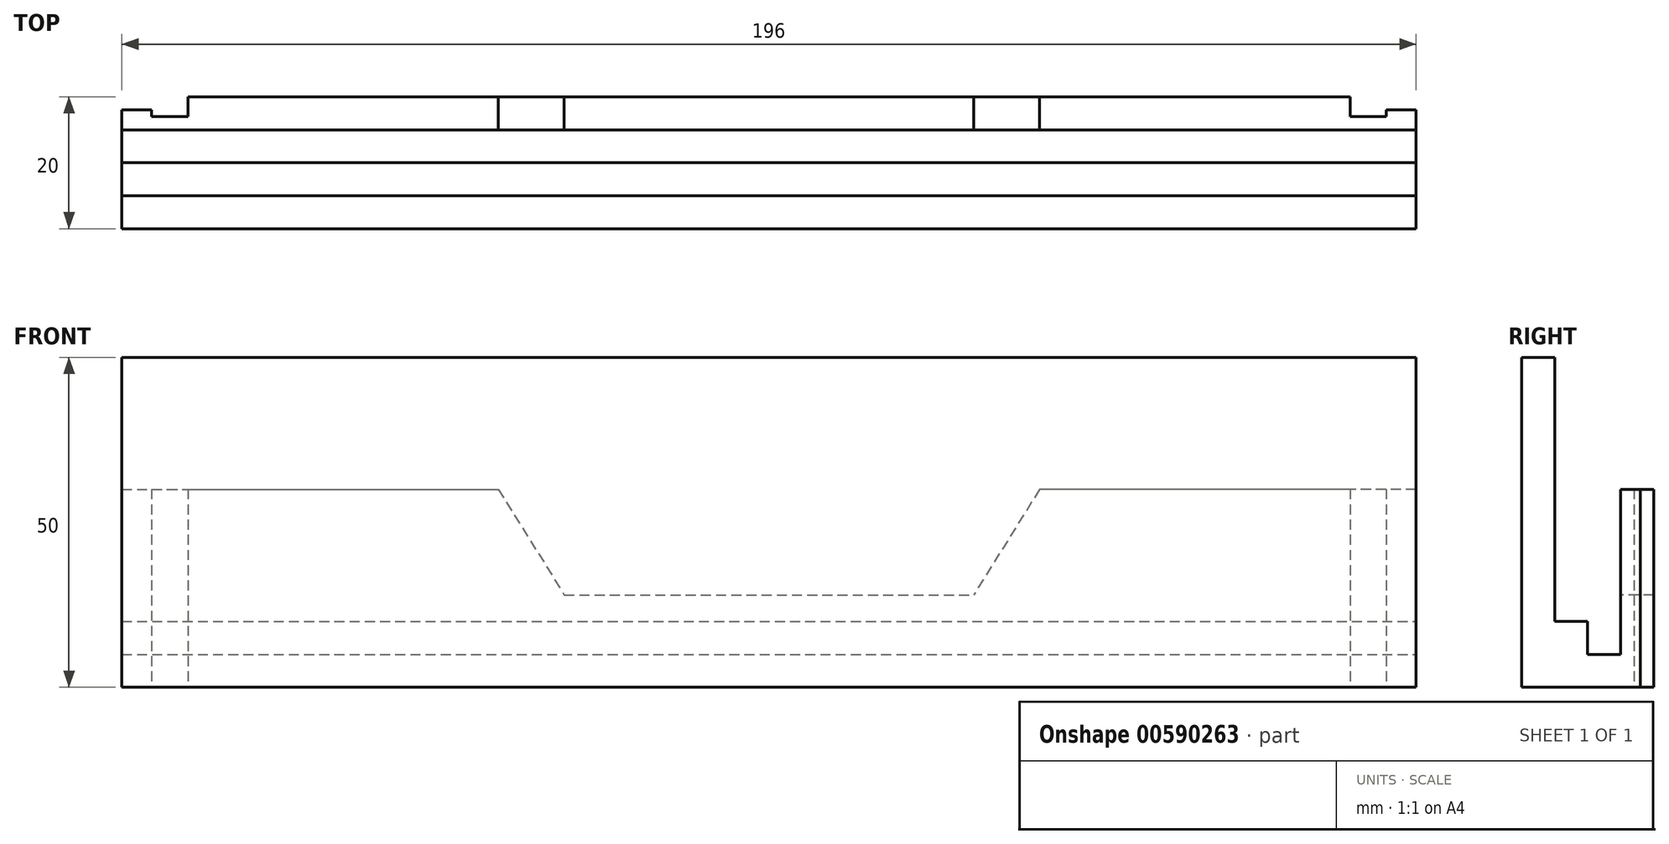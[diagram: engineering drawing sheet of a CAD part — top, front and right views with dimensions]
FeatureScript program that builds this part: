
annotation { "Feature Type Name" : "Feature", "Feature Type Description" : "" }
export const myFeature = defineFeature(function(context is Context, id is Id, definition is map)
    precondition{}
    {
        {
            var Q0;
            Q0=qCreatedBy(makeId("Top.planeOp"),FACE);
            var sketch = newSketch(context, id + "F0", { "sketchPlane" : qUnion([Q0])});
            skLineSegment(sketch, "E0.bottom", {"start": v(0, 0) * mm, "end": v(196, 0) * mm});
            skLineSegment(sketch, "E0.top", {"start": v(0, 5) * mm, "end": v(196, 5) * mm});
            skLineSegment(sketch, "E0.left", {"start": v(0, 0) * mm, "end": v(0, 5) * mm});
            skLineSegment(sketch, "E0.right", {"start": v(196, 0) * mm, "end": v(196, 5) * mm});
            skSolve(sketch);
        }
        {
            var Q0;
            Q0 = qSketchRegion(id + "F0", true);
            extrude(context, id + "F1", {"entities" : qUnion([Q0]), "depth" : 50 * mm, "offsetDistance" : 25 * mm});
        }
        {
            var Q0;
            Q0=qCreatedBy(makeId("Top.planeOp"),FACE);
            var sketch = newSketch(context, id + "F2", { "sketchPlane" : qUnion([Q0])});
            skLineSegment(sketch, "E1.bottom", {"start": v(0, 5) * mm, "end": v(196, 5) * mm});
            skLineSegment(sketch, "E1.top", {"start": v(0, 10) * mm, "end": v(196, 10) * mm});
            skLineSegment(sketch, "E1.left", {"start": v(0, 5) * mm, "end": v(0, 10) * mm});
            skLineSegment(sketch, "E1.right", {"start": v(196, 5) * mm, "end": v(196, 10) * mm});
            skSolve(sketch);
        }
        {
            var Q0;
            Q0 = qSketchRegion(id + "F2", true);
            extrude(context, id + "F3", {"entities" : qUnion([Q0]), "operationType" : NewBodyOperationType.ADD, "depth" : 10 * mm, "offsetDistance" : 25 * mm});
        }
        {
            var Q0;
            Q0=qCreatedBy(makeId("Top.planeOp"),FACE);
            var sketch = newSketch(context, id + "F4", { "sketchPlane" : qUnion([Q0])});
            skLineSegment(sketch, "E2.bottom", {"start": v(0, 10) * mm, "end": v(196, 10) * mm});
            skLineSegment(sketch, "E2.top", {"start": v(0, 15) * mm, "end": v(196, 15) * mm});
            skLineSegment(sketch, "E2.left", {"start": v(0, 10) * mm, "end": v(0, 15) * mm});
            skLineSegment(sketch, "E2.right", {"start": v(196, 10) * mm, "end": v(196, 15) * mm});
            skSolve(sketch);
        }
        {
            var Q0;
            Q0 = qSketchRegion(id + "F4", true);
            extrude(context, id + "F5", {"entities" : qUnion([Q0]), "operationType" : NewBodyOperationType.ADD, "depth" : 5 * mm, "offsetDistance" : 25 * mm});
        }
        {
            var Q0;
            Q0=qCreatedBy(makeId("Top.planeOp"),FACE);
            var sketch = newSketch(context, id + "F6", { "sketchPlane" : qUnion([Q0])});
            skLineSegment(sketch, "E3.bottom", {"start": v(0, 15) * mm, "end": v(4.5, 15) * mm});
            skLineSegment(sketch, "E3.top", {"start": v(0, 18) * mm, "end": v(4.5, 18) * mm});
            skLineSegment(sketch, "E3.left", {"start": v(0, 15) * mm, "end": v(0, 18) * mm});
            skLineSegment(sketch, "E3.right", {"start": v(4.5, 15) * mm, "end": v(4.5, 18) * mm});
            skLineSegment(sketch, "E4.bottom", {"start": v(4.5, 15) * mm, "end": v(10, 15) * mm});
            skLineSegment(sketch, "E4.top", {"start": v(4.5, 17) * mm, "end": v(10, 17) * mm});
            skLineSegment(sketch, "E4.left", {"start": v(4.5, 15) * mm, "end": v(4.5, 17) * mm});
            skLineSegment(sketch, "E4.right", {"start": v(10, 15) * mm, "end": v(10, 17) * mm});
            skLineSegment(sketch, "E5.bottom", {"start": v(10, 15) * mm, "end": v(57, 15) * mm});
            skLineSegment(sketch, "E5.top", {"start": v(10, 20) * mm, "end": v(57, 20) * mm});
            skLineSegment(sketch, "E5.left", {"start": v(10, 15) * mm, "end": v(10, 20) * mm});
            skLineSegment(sketch, "E5.right", {"start": v(57, 15) * mm, "end": v(57, 20) * mm});
            skLineSegment(sketch, "E6.bottom", {"start": v(196, 15) * mm, "end": v(191.5, 15) * mm});
            skLineSegment(sketch, "E6.top", {"start": v(196, 18) * mm, "end": v(191.5, 18) * mm});
            skLineSegment(sketch, "E6.left", {"start": v(196, 15) * mm, "end": v(196, 18) * mm});
            skLineSegment(sketch, "E6.right", {"start": v(191.5, 15) * mm, "end": v(191.5, 18) * mm});
            skLineSegment(sketch, "E7.bottom", {"start": v(191.5, 15) * mm, "end": v(186, 15) * mm});
            skLineSegment(sketch, "E7.top", {"start": v(191.5, 17) * mm, "end": v(186, 17) * mm});
            skLineSegment(sketch, "E7.left", {"start": v(191.5, 15) * mm, "end": v(191.5, 17) * mm});
            skLineSegment(sketch, "E7.right", {"start": v(186, 15) * mm, "end": v(186, 17) * mm});
            skLineSegment(sketch, "E8.bottom", {"start": v(186, 15) * mm, "end": v(139, 15) * mm});
            skLineSegment(sketch, "E8.top", {"start": v(186, 20) * mm, "end": v(139, 20) * mm});
            skLineSegment(sketch, "E8.left", {"start": v(186, 15) * mm, "end": v(186, 20) * mm});
            skLineSegment(sketch, "E8.right", {"start": v(139, 15) * mm, "end": v(139, 20) * mm});
            skSolve(sketch);
        }
        {
            var Q0;
            Q0 = qSketchRegion(id + "F6", true);
            extrude(context, id + "F7", {"entities" : qUnion([Q0]), "operationType" : NewBodyOperationType.ADD, "depth" : 30 * mm, "offsetDistance" : 25 * mm});
        }
        {
            var Q0;
            Q0=makeQuery(id+"F5.opExtrude","SWEPT_FACE",FACE,{"disambiguationData":[OSD([sQuery(id+"F4.wireOp",EDGE,"E2.top")])]});
            var sketch = newSketch(context, id + "F8", { "sketchPlane" : qUnion([Q0])});
            skLineSegment(sketch, "E9.bottom", {"start": v(-57, 0) * mm, "end": v(-139, 0) * mm});
            skLineSegment(sketch, "E9.top", {"start": v(-57, 14) * mm, "end": v(-139, 14) * mm});
            skLineSegment(sketch, "E9.left", {"start": v(-57, 0) * mm, "end": v(-57, 14) * mm});
            skLineSegment(sketch, "E9.right", {"start": v(-139, 0) * mm, "end": v(-139, 14) * mm});
            skLineSegment(sketch, "E10", {"start": v(-57, 14) * mm, "end": v(-57, 30) * mm});
            skLineSegment(sketch, "E11", {"start": v(-57, 30) * mm, "end": v(-67, 14) * mm});
            skLineSegment(sketch, "E12", {"start": v(-67, 14) * mm, "end": v(-57, 14) * mm});
            skLineSegment(sketch, "E13", {"start": v(-139, 14) * mm, "end": v(-139, 30) * mm});
            skLineSegment(sketch, "E14", {"start": v(-139, 30) * mm, "end": v(-129, 14) * mm});
            skLineSegment(sketch, "E15", {"start": v(-129, 14) * mm, "end": v(-139, 14) * mm});
            skSolve(sketch);
        }
        {
            var Q0;
            Q0 = qSketchRegion(id + "F8", true);
            extrude(context, id + "F9", {"entities" : qUnion([Q0]), "operationType" : NewBodyOperationType.ADD, "depth" : 5 * mm, "offsetDistance" : 25 * mm});
        }
    });
